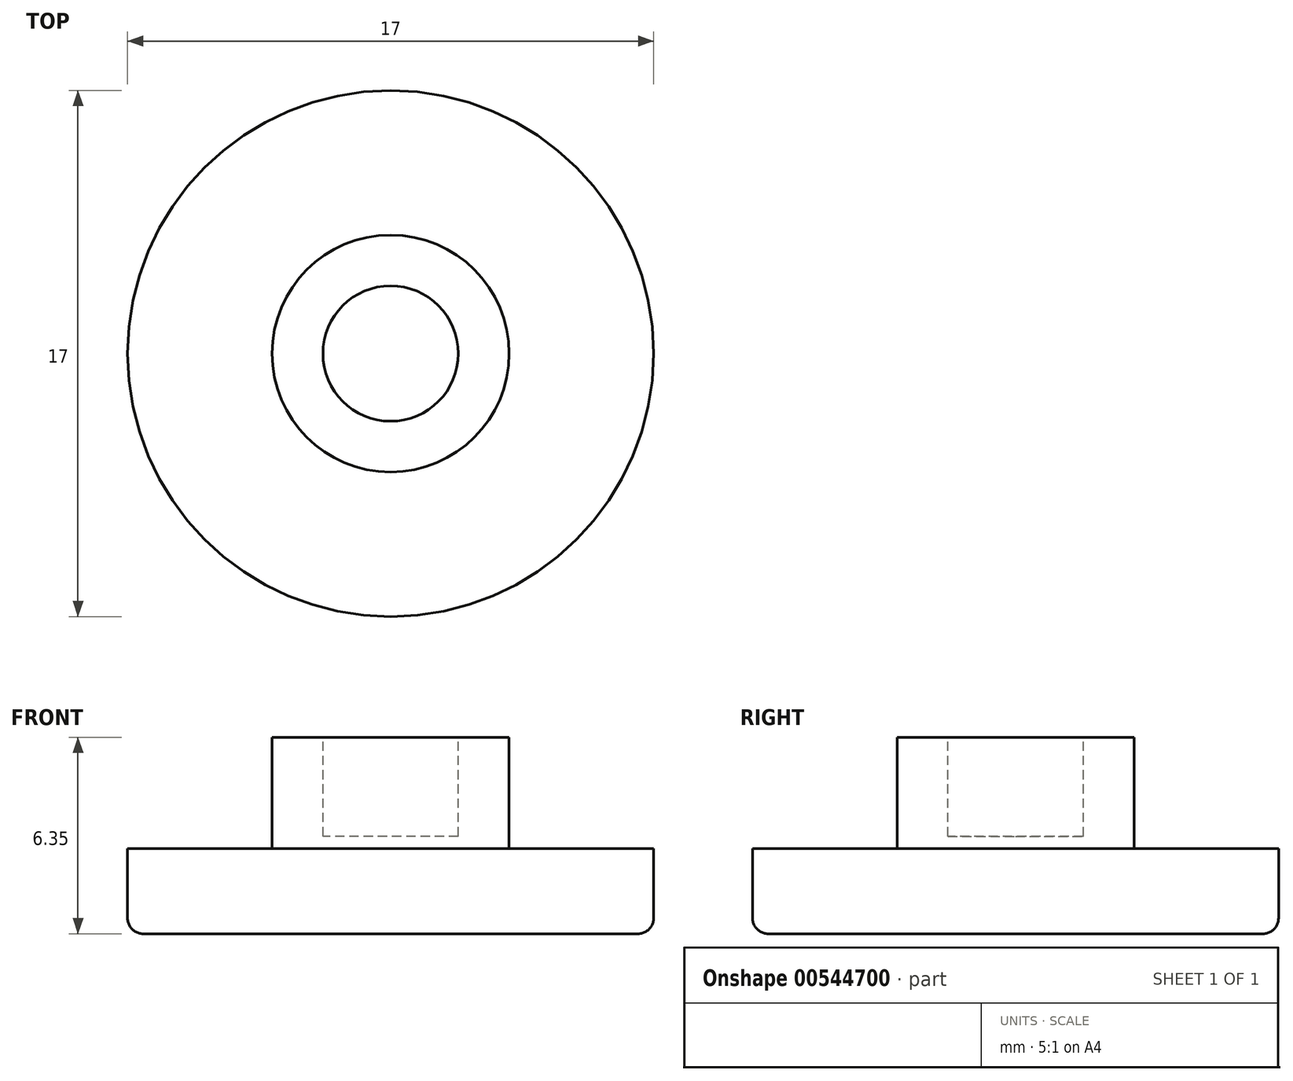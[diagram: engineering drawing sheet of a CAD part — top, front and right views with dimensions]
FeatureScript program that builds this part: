
annotation { "Feature Type Name" : "Feature", "Feature Type Description" : "" }
export const myFeature = defineFeature(function(context is Context, id is Id, definition is map)
    precondition{}
    {
        {
            var Q0;
            Q0=qCreatedBy(makeId("Top.planeOp"),FACE);
            var sketch = newSketch(context, id + "F0", { "sketchPlane" : qUnion([Q0])});
            skCircle(sketch, "E0", {"center": v(0, 0) * mm, "radius": 8.5 * mm});
            skSolve(sketch);
        }
        {
            var Q0;
            Q0=makeQuery(id+"F0.imprint","IMPRINT",FACE,{"disambiguationData":[TD([[makeQuery(id+"F0.imprint","IMPRINT",EDGE,{"derivedFrom":sQuery(id+"F0.wireOp",EDGE,"E0")}),1.0]])]});
            extrude(context, id + "F1", {"entities" : qUnion([Q0]), "depth" : 2.75 * mm, "offsetDistance" : 25 * mm});
        }
        {
            var Q0;
            Q0=makeQuery(id+"F1.opExtrude","CAP_FACE",FACE,{"disambiguationData":[OSD([sQuery(id+"F0.wireOp",EDGE,"E0")])],"isStart":false});
            var sketch = newSketch(context, id + "F2", { "sketchPlane" : qUnion([Q0])});
            skCircle(sketch, "E1", {"center": v(0, 0) * mm, "radius": 3.83 * mm});
            skSolve(sketch);
        }
        {
            var Q0;
            Q0 = qSketchRegion(id + "F2", true);
            extrude(context, id + "F3", {"entities" : qUnion([Q0]), "operationType" : NewBodyOperationType.ADD, "depth" : 3.6 * mm, "offsetDistance" : 25 * mm});
        }
        {
            var Q0;
            Q0=makeQuery(id+"F3.opExtrude","CAP_FACE",FACE,{"disambiguationData":[OSD([sQuery(id+"F2.wireOp",EDGE,"E1")])],"isStart":false});
            var sketch = newSketch(context, id + "F4", { "sketchPlane" : qUnion([Q0])});
            skCircle(sketch, "E2", {"center": v(0, 0) * mm, "radius": 2.19 * mm});
            skSolve(sketch);
        }
        {
            var Q0;
            Q0=makeQuery(id+"F4.imprint","IMPRINT",FACE,{"disambiguationData":[TD([[makeQuery(id+"F4.imprint","IMPRINT",EDGE,{"derivedFrom":sQuery(id+"F4.wireOp",EDGE,"E2")}),1.0]])]});
            extrude(context, id + "F5", {"entities" : qUnion([Q0]), "operationType" : NewBodyOperationType.REMOVE, "oppositeDirection" : true, "depth" : 3.2 * mm, "offsetDistance" : 25 * mm});
        }
        {
            var Q0;
            Q0=makeQuery(id+"F1.opExtrude","CAP_EDGE",EDGE,{"disambiguationData":[OSD([sQuery(id+"F0.wireOp",EDGE,"E0")])],"isStart":true});
            fillet(context, id + "F6", {"entities" : qUnion([Q0]), "radius" : .5 * mm, "tangentPropagation" : true, "allowEdgeOverflow" : false});
        }
    });
